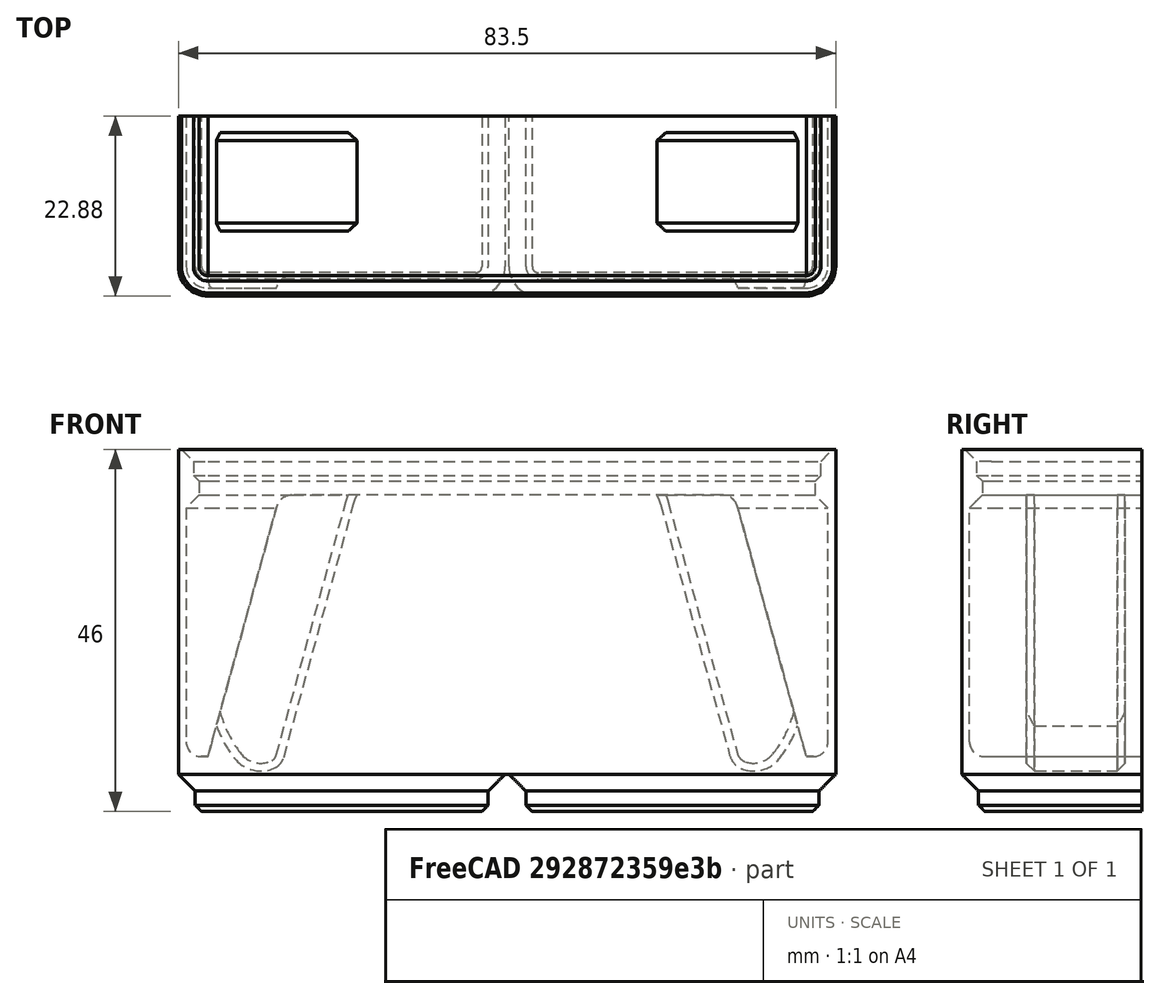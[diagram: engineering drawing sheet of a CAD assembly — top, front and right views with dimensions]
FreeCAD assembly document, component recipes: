
FREECAD ASSEMBLY — COMPONENT RECIPES ("clamp-holder")

This assembly document has 7 components, labeled P0..P6 below (a component is one placed body or linked part). 7 of them carry a construction recipe — the FreeCAD feature program that regenerates the part from scratch, quoted from this document or its linked companion documents; the rest are supplied as boundary geometry only. No exploded tour is included for this assembly.
COMPONENT P0 — recipe-attached ("template", modeled in this document).
Construction recipe (the document's own serialized feature program — sketch geometry with constraints, then the solid features built on it; lengths are millimeters unless a unit is written):

FEATURE [PartDesign::Plane] DatumPlane  label="orientation"
  AttachmentOffset = pos=(0,0,21) rot=(0,0,1;0rad)
  AttachmentSupport = -> [YZ_Plane]
  Length = 148.398
  MapMode = 5
  Placement = pos=(21,0,0) rot=(0.57735,0.57735,0.57735;2.0944rad)
  ResizeMode = 0
  Width = 85.6475
FEATURE [PartDesign::FeaturePython] SimpleStorageBin  # WARN: FeaturePython — macro-defined, semantics opaque (R4)
  BaseProfileBottomChamfer = 0.8
  BaseProfileHeight = 4.75
  BaseProfileTopChamfer = 2.15
  BaseProfileVerticalSection = 1.8
  BinBottomRadius = 0.8
  BinOuterRadius = 3.75
  BinUnit = 41.5
  BinVerticalRadius = 1.6
  CustomHeight = 42
  DividerThickness = 1.2
  GridSize = 42
  HeightUnitValue = 7
  HeightUnits = 6
  InsideFilletRadius = 1.85
  LabelShelfLength = 42
  LabelShelfPlacement = 0
  LabelShelfStyle = 0
  LabelShelfVerticalThickness = 1.2
  LabelShelfWidth = 12
  MagnetHoleDepth = 2.4
  MagnetHoleDiameter = 6.5
  MagnetHoleDistanceFromEdge = 8
  MagnetHoles = false
  NonStandardHeight = false
  Scoop = false
  ScoopRadius = 21
  ScrewHoleDepth = 6
  ScrewHoleDiameter = 3
  ScrewHoles = false
  SequentialBridgingLayerHeight = 0.2
  StackingLip = true
  StackingLipBottomChamfer = 0.7
  StackingLipTopChamfer = 1.5
  StackingLipTopLedge = 0.4
  StackingLipVerticalSection = 1.8
  Suppressed = false
  Tolerance = 0.25
  TotalHeight = 42
  UsableHeight = 35
  WallThickness = 1
  version = 0.6.0
  xDividerHeight = 0
  xDividers = 0
  xGridUnits = 2
  xTotalWidth = 83.5
  yDividerHeight = 0
  yDividers = 0
  yGridUnits = 3
  yTotalWidth = 125.5
FEATURE [Sketcher::SketchObject] Sketch
  ArcFitTolerance = 1e-06
  AttachmentSupport = -> [SimpleStorageBin]
  ExternalGeometry = -> [SimpleStorageBin]
  FullyConstrained = true
  MakeInternals = false
  MapMode = 5
  Placement = pos=(0,-20.75,0) rot=(1,0,0;1.5708rad)
  sketch-geometry (8):
    g0: LineSegment StartX=59 StartY=-35 StartZ=0 EndX=50.2711 EndY=-3.26952 EndZ=0
    g1: LineSegment StartX=-17 StartY=-35 StartZ=0 EndX=-8.27113 EndY=-3.26952 EndZ=0
    g2: LineSegment StartX=-17 StartY=-35 StartZ=0 EndX=59 EndY=-35 EndZ=0
    g3: LineSegment StartX=48.3428 StartY=-1.8 StartZ=0 EndX=-6.34276 EndY=-1.8 EndZ=0
    g4: ArcOfCircle CenterX=-6.34276 CenterY=-3.8 CenterZ=0 NormalX=0 NormalY=0 NormalZ=1 AngleXU=0 Radius=2 StartAngle=1.5708 EndAngle=2.87314
    g5: GeomPoint [constr] X=-7.86687 Y=-1.8 Z=0
    g6: ArcOfCircle CenterX=48.3428 CenterY=-3.8 CenterZ=0 NormalX=0 NormalY=0 NormalZ=1 AngleXU=0 Radius=2 StartAngle=0.268454 EndAngle=1.5708
    g7: GeomPoint [constr] X=49.8669 Y=-1.8 Z=0
  constraints (18):
    c: Coincident(g0,g-3)
    c: PointOnObject(g7,g-4)
    c: Parallel(g-5,g0)
    c: Coincident(g1,g-3)
    c: PointOnObject(g5,g-4)
    c: Parallel(g1,g-8)
    c: Coincident(g2,g1)
    c: Coincident(g2,g0)
    c: PointOnObject(g5,g3)
    c: PointOnObject(g5,g1)
    c: Tangent(g3,g4) = -1.5708
    c: Tangent(g1,g4) = 1.5708
    c: PointOnObject(g7,g3)
    c: PointOnObject(g7,g0)
    c: Tangent(g3,g6) = -1.5708
    c: Tangent(g0,g6) = -1.5708
    c: Equal(g6,g4)
    c: Radius(g6) = 2
FEATURE [PartDesign::SubShapeBinder] Binder
  BindCopyOnChange = 0
  BindMode = 0
  ClaimChildren = false
  Context = -> Body [Binder.]
  Fuse = false
  MakeFace = true
  OffsetFill = false
  OffsetIntersection = false
  OffsetJoinType = 0
  OffsetOpenResult = false
  PartialLoad = false
  Relative = true
  Support = -> [Link]
  _Version = 2
FEATURE [PartDesign::Pad] Pad
  BaseFeature = -> SimpleStorageBin
  Direction = (0,-1,2e-16)
  Length = 10
  Length2 = 10
  Profile = -> Sketch
  ReferenceAxis = -> Sketch [N_Axis]
  Suppressed = false
  Type = 3
  UpToFace = -> SimpleStorageBin [Face189]
FEATURE [PartDesign::Body] Body  label="bin"
  AllowCompound = false
  Group = -> [DatumPlane,Binder,SimpleStorageBin,Sketch,Pad]
  Origin = -> Origin
  Tip = -> Pad
COMPONENT P1 — same part as P0; its construction recipe is shown at P0.
COMPONENT P2 — same part as P0; its construction recipe is shown at P0.
COMPONENT P3 — same part as P0; its construction recipe is shown at P0.
COMPONENT P4 — same part as P0; its construction recipe is shown at P0.
COMPONENT P5 — same part as P0; its construction recipe is shown at P0.
COMPONENT P6 — same part as P0; its construction recipe is shown at P0.
PROVENANCE & LICENSES
A FreeCAD (.FCStd) document from a public repository crawl; recipes are the document's own serialized feature recipes (and, for linked parts, companion documents' recipes).
License: unknown-license-file.
